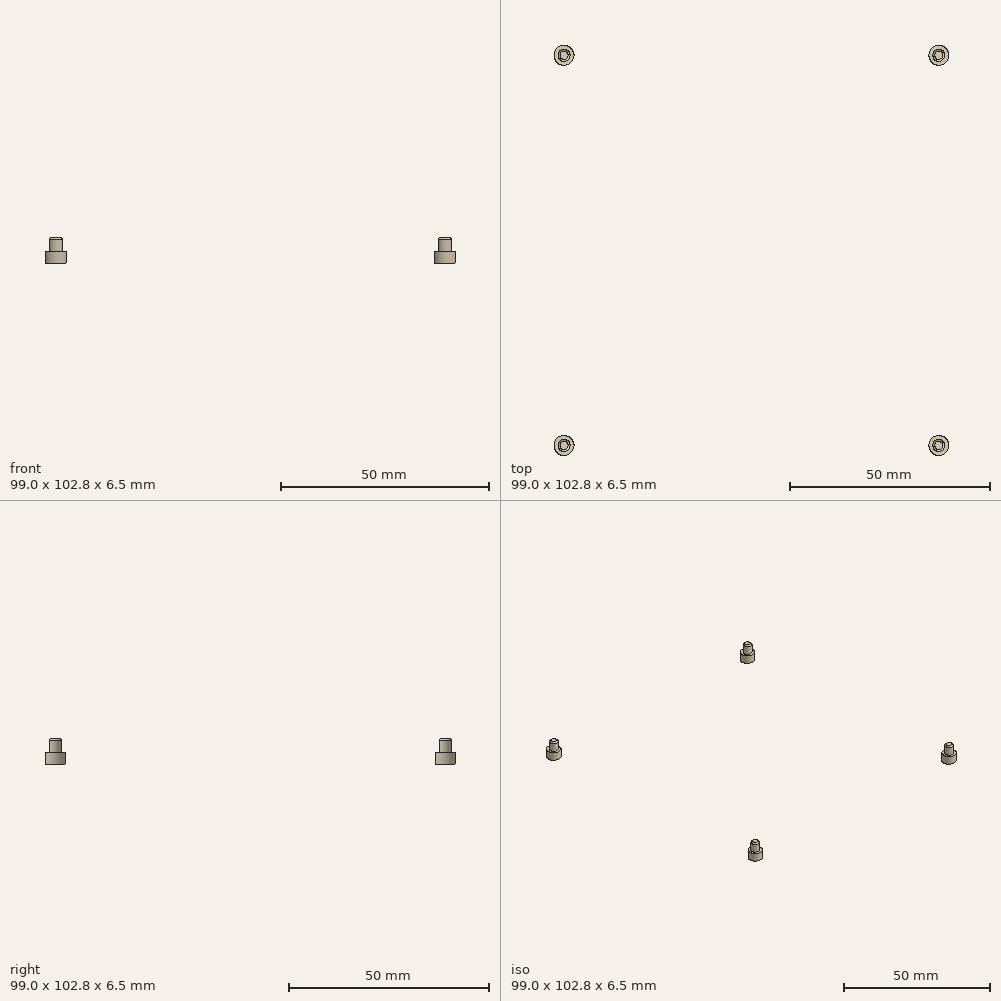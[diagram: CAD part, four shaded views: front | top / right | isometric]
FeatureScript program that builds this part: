
annotation { "Feature Type Name" : "Feature", "Feature Type Description" : "" }
export const myFeature = defineFeature(function(context is Context, id is Id, definition is map)
    precondition{}
    {
        {
            var Q0;
            Q0=qCreatedBy(makeId("Top.planeOp"),FACE);
            var sketch = newSketch(context, id + "F0", { "sketchPlane" : qUnion([Q0])});
            skLineSegment(sketch, "E0.bottom", {"start": v(-50.8, 52.7) * mm, "end": v(50.8, 52.7) * mm});
            skLineSegment(sketch, "E0.top", {"start": v(-50.8, -52.7) * mm, "end": v(50.8, -52.7) * mm});
            skLineSegment(sketch, "E0.left", {"start": v(-50.8, 52.7) * mm, "end": v(-50.8, -52.7) * mm});
            skLineSegment(sketch, "E0.right", {"start": v(50.8, 52.7) * mm, "end": v(50.8, -52.7) * mm});
            skPoint(sketch, "E0.middle", {"position": v(0, 0) * mm});
            skCircle(sketch, "E1", {"center": v(-46.99, 48.9) * mm, "radius": 1.52 * mm});
            skCircle(sketch, "E2", {"center": v(47, 48.9) * mm, "radius": 1.52 * mm});
            skCircle(sketch, "E3", {"center": v(46.99, -48.9) * mm, "radius": 1.52 * mm});
            skCircle(sketch, "E4", {"center": v(-47, -48.9) * mm, "radius": 1.52 * mm});
            skPoint(sketch, "E5.middle", {"position": v(-36.32, -52.7) * mm});
            skSolve(sketch);
        }
        {
            var Q0;
            Q0=makeQuery(id+"F0.imprint","IMPRINT",FACE,{"disambiguationData":[TD([[makeQuery(id+"F0.imprint","IMPRINT",EDGE,{"derivedFrom":sQuery(id+"F0.wireOp",EDGE,"E2")}),1.0]])]});
            var Q1;
            Q1=makeQuery(id+"F0.imprint","IMPRINT",FACE,{"disambiguationData":[TD([[makeQuery(id+"F0.imprint","IMPRINT",EDGE,{"derivedFrom":sQuery(id+"F0.wireOp",EDGE,"E1")}),1.0]])]});
            var Q2;
            Q2=makeQuery(id+"F0.imprint","IMPRINT",FACE,{"disambiguationData":[TD([[makeQuery(id+"F0.imprint","IMPRINT",EDGE,{"derivedFrom":sQuery(id+"F0.wireOp",EDGE,"E4")}),1.0]])]});
            var Q3;
            Q3=makeQuery(id+"F0.imprint","IMPRINT",FACE,{"disambiguationData":[TD([[makeQuery(id+"F0.imprint","IMPRINT",EDGE,{"derivedFrom":sQuery(id+"F0.wireOp",EDGE,"E3")}),1.0]])]});
            var Q4;
            Q4=sQuery(id+"F0.wireOp",EDGE,"E1");
            var Q5;
            Q5=sQuery(id+"F0.wireOp",EDGE,"E2");
            var Q6;
            Q6=sQuery(id+"F0.wireOp",EDGE,"E3");
            var Q7;
            Q7=sQuery(id+"F0.wireOp",EDGE,"E4");
            extrude(context, id + "F1", {"entities" : qUnion([Q0, Q1, Q2, Q3]), "surfaceEntities" : qUnion([Q4, Q5, Q6, Q7]), "depth" : 3.5 * mm});
        }
        {
            var Q0;
            Q0=makeQuery(id+"F0.imprint","IMPRINT",FACE,{"disambiguationData":[TD([[makeQuery(id+"F0.imprint","IMPRINT",EDGE,{"derivedFrom":sQuery(id+"F0.wireOp",EDGE,"E0.bottom")}),-1.0]])]});
            var sketch = newSketch(context, id + "F2", { "sketchPlane" : qUnion([Q0])});
            skCircle(sketch, "E6", {"center": v(-47, -48.9) * mm, "radius": 2.5 * mm});
            skCircle(sketch, "E7", {"center": v(46.99, -48.9) * mm, "radius": 2.5 * mm});
            skCircle(sketch, "E8", {"center": v(47, 48.9) * mm, "radius": 2.5 * mm});
            skCircle(sketch, "E9", {"center": v(-46.99, 48.9) * mm, "radius": 2.5 * mm});
            skSolve(sketch);
        }
        {
            var Q0;
            Q0=makeQuery(id+"F2.imprint","IMPRINT",FACE,{"disambiguationData":[TD([[makeQuery(id+"F2.imprint","IMPRINT",EDGE,{"derivedFrom":sQuery(id+"F2.wireOp",EDGE,"E6")}),1.0]])]});
            var Q1;
            Q1=makeQuery(id+"F2.imprint","IMPRINT",FACE,{"disambiguationData":[TD([[makeQuery(id+"F2.imprint","IMPRINT",EDGE,{"derivedFrom":makeQuery(id+"F0.imprint","IMPRINT",EDGE,{"derivedFrom":sQuery(id+"F0.wireOp",EDGE,"E4")})}),1.0]])]});
            var Q2;
            Q2=makeQuery(id+"F2.imprint","IMPRINT",FACE,{"disambiguationData":[TD([[makeQuery(id+"F2.imprint","IMPRINT",EDGE,{"derivedFrom":makeQuery(id+"F0.imprint","IMPRINT",EDGE,{"derivedFrom":sQuery(id+"F0.wireOp",EDGE,"E3")})}),1.0]])]});
            var Q3;
            Q3=makeQuery(id+"F2.imprint","IMPRINT",FACE,{"disambiguationData":[TD([[makeQuery(id+"F2.imprint","IMPRINT",EDGE,{"derivedFrom":sQuery(id+"F2.wireOp",EDGE,"E7")}),1.0]])]});
            var Q4;
            Q4=makeQuery(id+"F2.imprint","IMPRINT",FACE,{"disambiguationData":[TD([[makeQuery(id+"F2.imprint","IMPRINT",EDGE,{"derivedFrom":sQuery(id+"F2.wireOp",EDGE,"E9")}),1.0]])]});
            var Q5;
            Q5=makeQuery(id+"F2.imprint","IMPRINT",FACE,{"disambiguationData":[TD([[makeQuery(id+"F2.imprint","IMPRINT",EDGE,{"derivedFrom":makeQuery(id+"F0.imprint","IMPRINT",EDGE,{"derivedFrom":sQuery(id+"F0.wireOp",EDGE,"E1")})}),1.0]])]});
            var Q6;
            Q6=makeQuery(id+"F2.imprint","IMPRINT",FACE,{"disambiguationData":[TD([[makeQuery(id+"F2.imprint","IMPRINT",EDGE,{"derivedFrom":sQuery(id+"F2.wireOp",EDGE,"E8")}),1.0]])]});
            var Q7;
            Q7=makeQuery(id+"F2.imprint","IMPRINT",FACE,{"disambiguationData":[TD([[makeQuery(id+"F2.imprint","IMPRINT",EDGE,{"derivedFrom":makeQuery(id+"F0.imprint","IMPRINT",EDGE,{"derivedFrom":sQuery(id+"F0.wireOp",EDGE,"E2")})}),1.0]])]});
            extrude(context, id + "F3", {"entities" : qUnion([Q0, Q1, Q2, Q3, Q4, Q5, Q6, Q7]), "oppositeDirection" : true, "depth" : 3 * mm});
        }
        {
            var Q0;
            Q0=makeQuery(id+"F1.opExtrude","CAP_EDGE",EDGE,{"disambiguationData":[OSD([sQuery(id+"F0.wireOp",EDGE,"E4")])],"isStart":false});
            var Q1;
            Q1=makeQuery(id+"F1.opExtrude","CAP_EDGE",EDGE,{"disambiguationData":[OSD([sQuery(id+"F0.wireOp",EDGE,"E1")])],"isStart":false});
            var Q2;
            Q2=makeQuery(id+"F1.opExtrude","CAP_EDGE",EDGE,{"disambiguationData":[OSD([sQuery(id+"F0.wireOp",EDGE,"E2")])],"isStart":false});
            var Q3;
            Q3=makeQuery(id+"F1.opExtrude","CAP_EDGE",EDGE,{"disambiguationData":[OSD([sQuery(id+"F0.wireOp",EDGE,"E3")])],"isStart":false});
            chamfer(context, id + "F4", {"entities" : qUnion([Q0, Q1, Q2, Q3]), "width" : .5 * mm, "tangentPropagation" : true});
        }
    });
